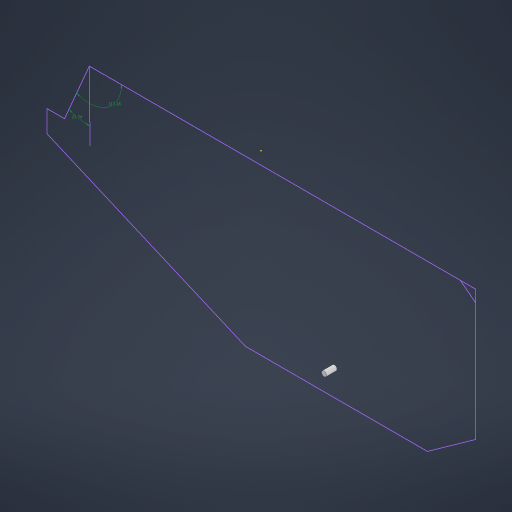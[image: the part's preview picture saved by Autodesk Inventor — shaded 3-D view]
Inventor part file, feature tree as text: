
AUTODESK INVENTOR PART (.ipt)
format: ipt  version: 2024 (Build 280153000, 153)  size: 267,264 bytes
history: native  units: in
note: dims shown in document units (in); Inventor stores cm internally (conversion verified against a paired STEP export)
features: reference x13, sketch x7, plane x6, other x5, extrude x5, projected_geometry x3
ambient origin geometry x8: Origin, YZ Plane, XZ Plane, XY Plane, X Axis, Y Axis, Z Axis, Center Point
bodies: Solid1 (feature_tree)
feature tree (39):
  plane  "Work Plane1"
  other  "Work Point1"
  extrude  "Extrusion1"  Depth=12.0in
  plane  "Work Plane6"
  extrude  "Extrusion2"  Depth=0.4626in
  extrude  "Extrusion3"  Depth=1.2205in
  plane  "Work Plane2"
  sketch  "Sketch8"  dims[d6=1.0in d7=0.0in d8=1.0in d9=0.0in]
  plane  "Work Plane3"
  plane  "Work Plane4"
  plane  "Work Plane7"
  extrude  "Extrusion12"  Depth=1.0in TaperAngle=0.0deg
  extrude  "Extrusion13"  Depth=0.1378in TaperAngle=0.0deg
  sketch  "Sketch19"  dims[d50=0.1654in d54=10.0in d55=0.1969in d56=0.0in d57=0.1654in d58=2.0in d59=3.5433in d61=360.0deg d63=0.1969in d64=0.0in d75=12.0in d76=0.7776in d77=0.1631in]
  sketch  "Sketch2"  dims[d0=0.0157in d1=12.0in]
  reference  "Reference1"
  reference  "Reference2"
  reference  "Reference3"
  reference  "Reference4"
  reference  "Reference5"
  reference  "Reference6"
  reference  "Reference7"
  sketch  "Sketch3"  dims[d2=0.0197in d3=0.4626in]
  reference  "Reference8"
  sketch  "Sketch6"  dims[d4=0.0787in d5=1.2205in]
  projected_geometry  "Projected Loop1"
  reference  "Reference9"
  reference  "Reference10"
  reference  "Reference11"
  reference  "Reference12"
  reference  "Reference13"
  sketch  "Sketch16"  dims[d10=0.2559in d11=0.1378in d12=0.0in]
  projected_geometry  "Projected Loop14"
  sketch  "Sketch17"  dims[d35=60.0deg]
  projected_geometry  "Projected Loop15"
  other  "<userpath>\Desktop\SeniorDesign\Head_Assembly.iam"
  other  "Head_Assembly.iam"
  other  "Emeet_Camera:1"
  other  "Assembly1"
